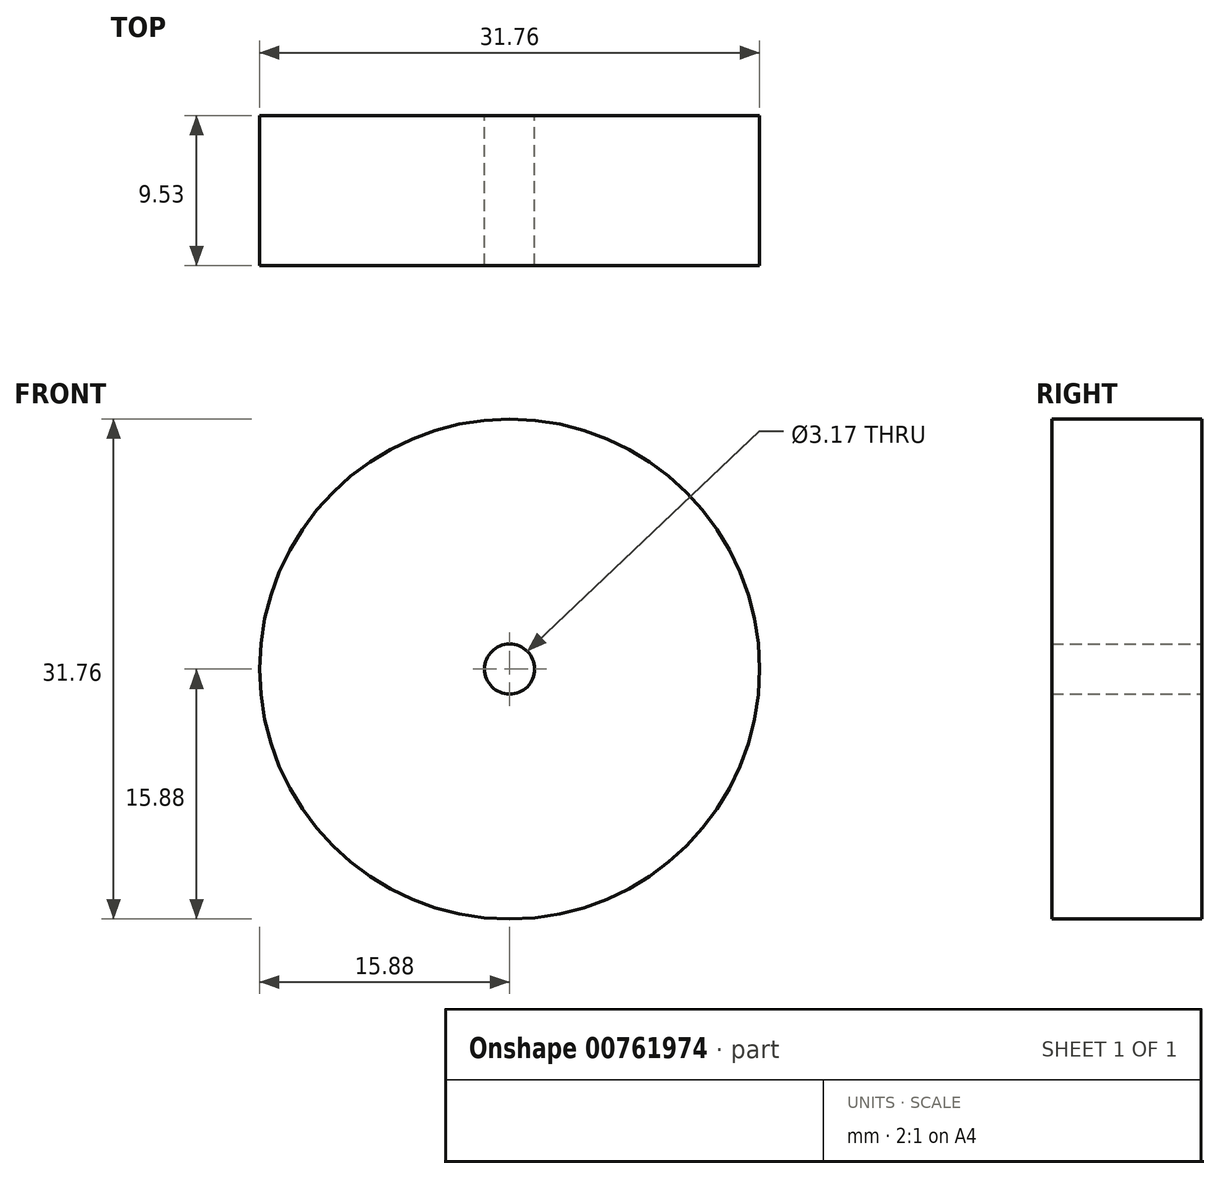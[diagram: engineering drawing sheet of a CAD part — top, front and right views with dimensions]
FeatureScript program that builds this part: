
annotation { "Feature Type Name" : "Feature", "Feature Type Description" : "" }
export const myFeature = defineFeature(function(context is Context, id is Id, definition is map)
    precondition{}
    {
        {
            var Q0;
            Q0=qCreatedBy(makeId("Front.planeOp"),FACE);
            var sketch = newSketch(context, id + "F0", { "sketchPlane" : qUnion([Q0])});
            skCircle(sketch, "E0", {"center": v(0, 0) * mm, "radius": 15.88 * mm});
            skCircle(sketch, "E1", {"center": v(0, 0) * mm, "radius": 1.59 * mm});
            skSolve(sketch);
        }
        {
            var Q0;
            Q0 = qSketchRegion(id + "F0", true);
            extrude(context, id + "F1", {"entities" : qUnion([Q0]), "depth" : 9.52 * mm, "offsetDistance" : 25.4 * mm});
        }
    });
